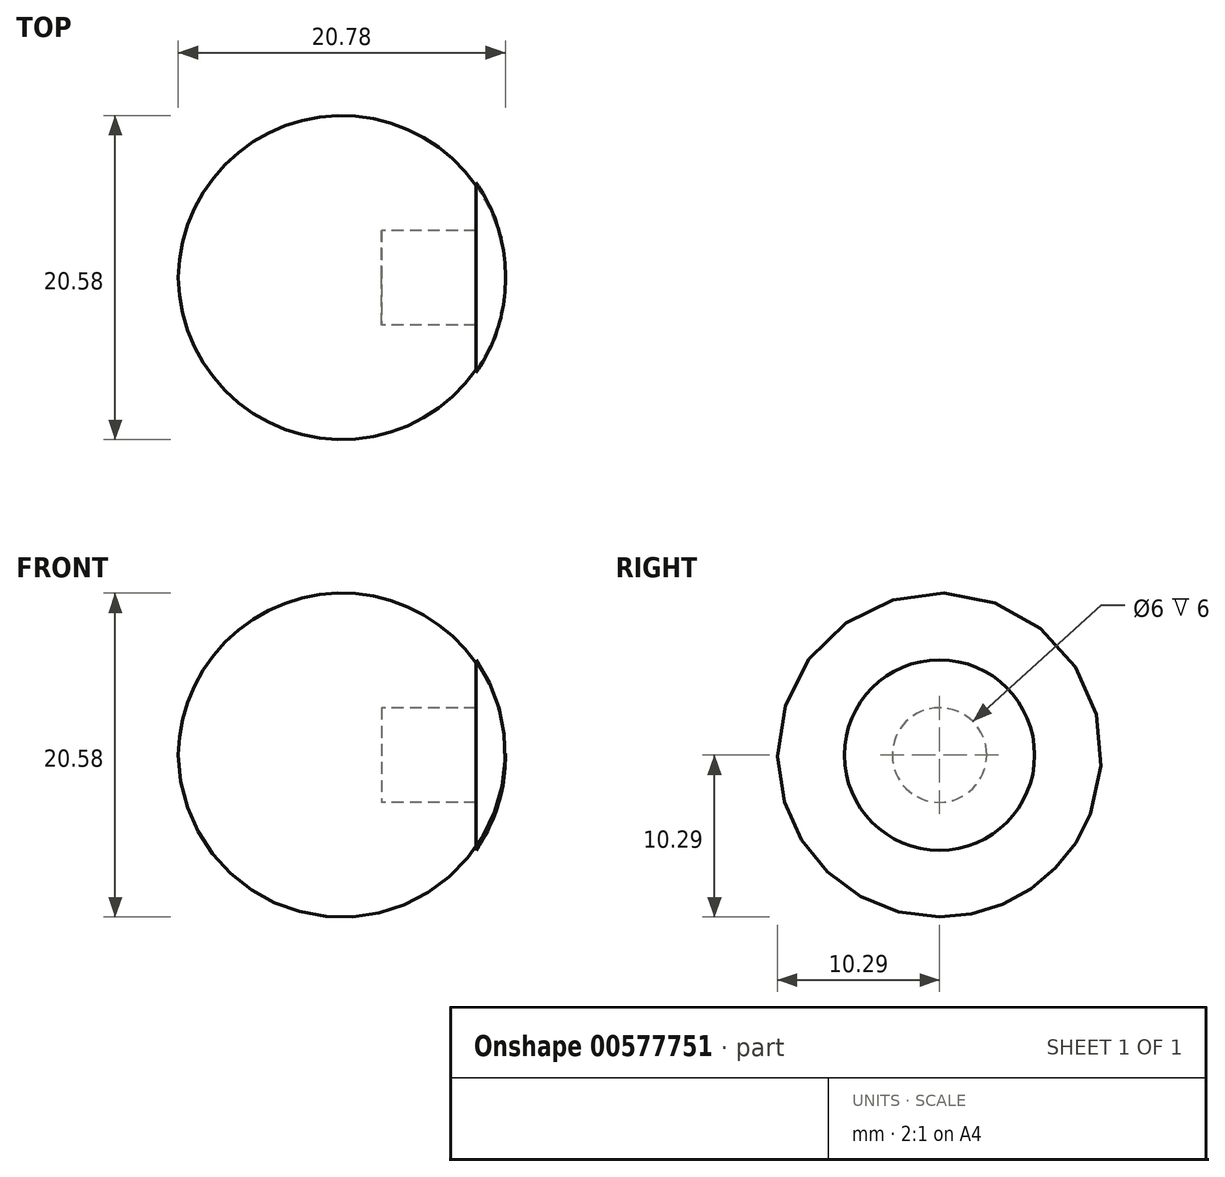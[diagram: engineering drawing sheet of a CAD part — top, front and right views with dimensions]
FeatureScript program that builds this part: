
annotation { "Feature Type Name" : "Feature", "Feature Type Description" : "" }
export const myFeature = defineFeature(function(context is Context, id is Id, definition is map)
    precondition{}
    {
        {
            var Q0;
            Q0=qCreatedBy(makeId("Top.planeOp"),FACE);
            var sketch = newSketch(context, id + "F0", { "sketchPlane" : qUnion([Q0])});
            skLineSegment(sketch, "E0.bottom", {"start": v(0, 0) * mm, "end": v(6, 0) * mm});
            skLineSegment(sketch, "E0.top", {"start": v(0, 3) * mm, "end": v(6, 3) * mm});
            skLineSegment(sketch, "E0.left", {"start": v(0, 0) * mm, "end": v(0, 3) * mm});
            skLineSegment(sketch, "E0.right", {"start": v(6, 0) * mm, "end": v(6, 3) * mm});
            skArc(sketch, "E1", {"start": v(7.87, 0) * mm, "mid": v(7.4, 3.17) * mm, "end": v(6, 6.04) * mm});
            skLineSegment(sketch, "E2", {"start": v(6, 3) * mm, "end": v(6, 6.04) * mm});
            skLineSegment(sketch, "E3", {"start": v(6, 0) * mm, "end": v(7.87, 0) * mm});
            skSolve(sketch);
        }
        {
            var Q0;
            Q0 = qSketchRegion(id + "F0", true);
            var Q1;
            Q1=sQuery(id+"F0.wireOp",EDGE,"E0.bottom");
            revolve(context, id + "F1", {"entities" : qUnion([Q0]), "axis" : qUnion([Q1]), "revolveType" : RevolveType.FULL});
        }
    });
